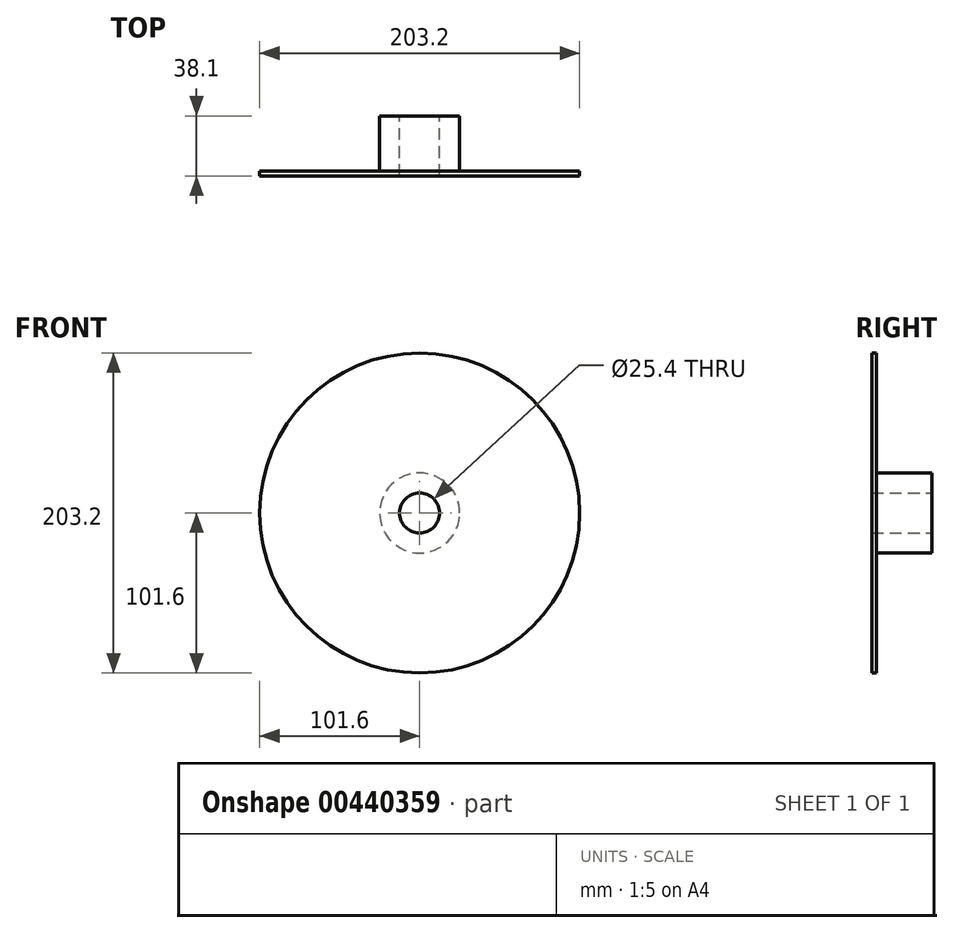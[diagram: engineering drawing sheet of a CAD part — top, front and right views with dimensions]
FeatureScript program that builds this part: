
annotation { "Feature Type Name" : "Feature", "Feature Type Description" : "" }
export const myFeature = defineFeature(function(context is Context, id is Id, definition is map)
    precondition{}
    {
        {
            var Q0;
            Q0=qCreatedBy(makeId("Front.planeOp"),FACE);
            var sketch = newSketch(context, id + "F0", { "sketchPlane" : qUnion([Q0])});
            skCircle(sketch, "E0", {"center": v(0, 0) * mm, "radius": 101.6 * mm});
            skSolve(sketch);
        }
        {
            var Q0;
            Q0=makeQuery(id+"F0.imprint","IMPRINT",FACE,{"disambiguationData":[TD([[makeQuery(id+"F0.imprint","IMPRINT",EDGE,{"derivedFrom":sQuery(id+"F0.wireOp",EDGE,"E0")}),1.0]])]});
            extrude(context, id + "F1", {"entities" : qUnion([Q0]), "endBound" : BoundingType.SYMMETRIC, "depth" : 3.17 * mm});
        }
        {
            var Q0;
            Q0=makeQuery(id+"F1.opExtrude","CAP_FACE",FACE,{"disambiguationData":[OSD([sQuery(id+"F0.wireOp",EDGE,"E0")])],"isStart":false});
            var sketch = newSketch(context, id + "F2", { "sketchPlane" : qUnion([Q0])});
            skCircle(sketch, "E1", {"center": v(0, 0) * mm, "radius": 25.4 * mm});
            skSolve(sketch);
        }
        {
            var Q0;
            Q0=makeQuery(id+"F2.imprint","IMPRINT",FACE,{"disambiguationData":[TD([[makeQuery(id+"F2.imprint","IMPRINT",EDGE,{"derivedFrom":sQuery(id+"F2.wireOp",EDGE,"E1")}),1.0]])]});
            extrude(context, id + "F3", {"entities" : qUnion([Q0]), "operationType" : NewBodyOperationType.ADD, "depth" : -38.1 * mm});
        }
        {
            var Q0;
            Q0=makeQuery(id+"F3.opExtrude","CAP_FACE",FACE,{"disambiguationData":[OSD([sQuery(id+"F2.wireOp",EDGE,"E1")])],"isStart":false});
            var sketch = newSketch(context, id + "F4", { "sketchPlane" : qUnion([Q0])});
            skCircle(sketch, "E2", {"center": v(0, 0) * mm, "radius": 12.7 * mm});
            skSolve(sketch);
        }
        {
            var Q0;
            Q0=makeQuery(id+"F4.imprint","IMPRINT",FACE,{"disambiguationData":[TD([[makeQuery(id+"F4.imprint","IMPRINT",EDGE,{"derivedFrom":sQuery(id+"F4.wireOp",EDGE,"E2")}),1.0]])]});
            extrude(context, id + "F5", {"entities" : qUnion([Q0]), "operationType" : NewBodyOperationType.REMOVE, "oppositeDirection" : true, "depth" : -63.5 * mm});
        }
        {
            var Q0;
            Q0=makeQuery(id+"F3.opExtrude","CAP_FACE",FACE,{"disambiguationData":[OSD([sQuery(id+"F2.wireOp",EDGE,"E1")])],"isStart":false});
            var sketch = newSketch(context, id + "F6", { "sketchPlane" : qUnion([Q0])});
            skCircle(sketch, "E3", {"center": v(0, 0) * mm, "radius": 12.7 * mm});
            skSolve(sketch);
        }
        {
            var Q0;
            Q0=makeQuery(id+"F6.imprint","IMPRINT",FACE,{"disambiguationData":[TD([[makeQuery(id+"F6.imprint","IMPRINT",EDGE,{"derivedFrom":sQuery(id+"F6.wireOp",EDGE,"E3")}),1.0]])]});
            extrude(context, id + "F7", {"entities" : qUnion([Q0]), "operationType" : NewBodyOperationType.REMOVE, "oppositeDirection" : true, "depth" : 63.5 * mm});
        }
    });
